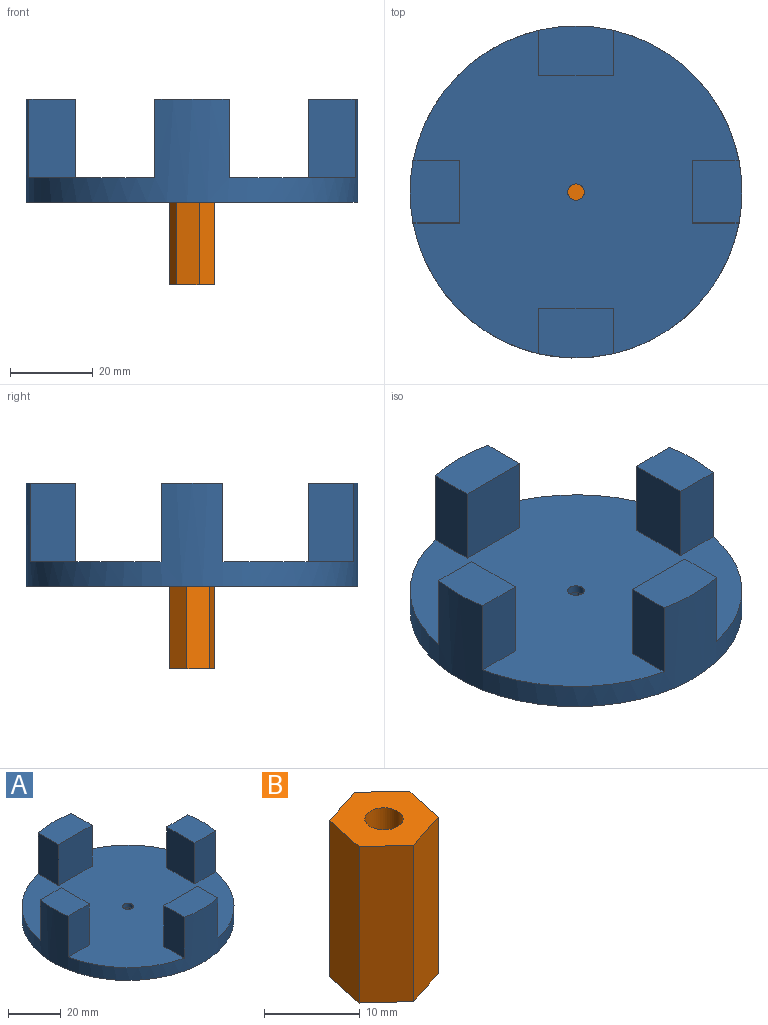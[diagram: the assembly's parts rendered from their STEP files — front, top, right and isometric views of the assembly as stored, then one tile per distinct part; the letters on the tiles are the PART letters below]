
ASSEMBLY  parts=2 mates=1
PART A: 27 faces, bbox 80.4x80.4x25 mm
  f0: plane 80.35x80.35mm, normal (0,0,-1), area 4987.5mm2, adj f2,f19,f20,f21,f22,f23,f24
  f1: plane 19x10.91mm, normal (1,0,0), area 207.2mm2, adj f2,f4,f5,f18
  f2: cylinder r=40.18mm len=80.35mm, axis (0,0,-1), area 2777.8mm2, adj f0,f1,f3,f5,f6,f8,f9,f10
  f3: plane 19x10.91mm, normal (-1,0,0), area 207.2mm2, adj f2,f4,f5,f18
  f4: plane 19x18mm, normal (0,-1,0), area 342mm2, adj f1,f3,f5,f18
  f5: plane 18x11.93mm, normal (0,0,1), area 208.6mm2, adj f1,f2,f3,f4
  f6: plane 19x10.91mm, normal (1,0,0), area 207.2mm2, adj f2,f7,f9,f18
  f7: plane 19x18mm, normal (0,1,0), area 342mm2, adj f6,f8,f9,f18
  f8: plane 19x10.91mm, normal (-1,0,0), area 207.2mm2, adj f2,f7,f9,f18
  f9: plane 18x11.93mm, normal (0,0,1), area 208.6mm2, adj f2,f6,f7,f8
  f10: plane 19x11.22mm, normal (0,1,0), area 213.2mm2, adj f2,f11,f13,f18
  f11: plane 19x15mm, normal (-1,0,0), area 285mm2, adj f10,f12,f13,f18
  f12: plane 19x11.22mm, normal (0,-1,0), area 213.2mm2, adj f2,f11,f13,f18
  f13: plane 15x11.93mm, normal (0,0,1), area 175.4mm2, adj f2,f10,f11,f12
  f14: plane 19x11.22mm, normal (0,1,0), area 213.2mm2, adj f2,f16,f17,f18
  f15: plane 19x11.22mm, normal (0,-1,0), area 213.2mm2, adj f2,f16,f17,f18
  f16: plane 19x15mm, normal (1,0,0), area 285mm2, adj f14,f15,f17,f18
  f17: plane 15x11.93mm, normal (0,0,1), area 175.4mm2, adj f2,f14,f15,f16
  f18: plane 78.94x78.31mm, normal (0,0,1), area 4290.6mm2, adj f1,f2,f3,f4,f6,f7,f8,f10
  f19: plane 5.41x4mm, normal (-0.3,-0.95,0), area 22.7mm2, adj f0,f20,f24,f25
  f20: plane 5.54x4mm, normal (-0.98,-0.21,0), area 22.7mm2, adj f0,f19,f21,f25
  f21: plane 4.19x4mm, normal (-0.67,0.74,0), area 22.7mm2, adj f0,f20,f22,f25
  f22: plane 5.41x4mm, normal (0.3,0.95,0), area 22.7mm2, adj f0,f21,f23,f25
  f23: plane 5.54x4mm, normal (0.98,0.21,0), area 22.7mm2, adj f0,f22,f24,f25
  f24: plane 4.19x4mm, normal (0.67,-0.74,0), area 22.7mm2, adj f0,f19,f23,f25
  f25: plane 11.08x10.81mm, normal (0,0,-1), area 71mm2, adj f19,f20,f21,f22,f23,f24,f26
  f26: cylinder r=2mm len=4mm, axis (0,0,-1), area 25.1mm2, adj f18,f25
PART B: 10 faces, bbox 10.8x11.1x20 mm
  f0: plane 20x5.41mm, normal (0.3,-0.95,0), area 113.4mm2, adj f1,f5,f6,f7
  f1: plane 20x5.54mm, normal (0.98,-0.21,0), area 113.4mm2, adj f0,f2,f6,f7
  f2: plane 20x4.19mm, normal (0.67,0.74,0), area 113.4mm2, adj f1,f3,f6,f7
  f3: plane 20x5.41mm, normal (-0.3,0.95,0), area 113.4mm2, adj f2,f4,f6,f7
  f4: plane 20x5.54mm, normal (-0.98,0.21,0), area 113.4mm2, adj f3,f5,f6,f7
  f5: plane 20x4.19mm, normal (-0.67,-0.74,0), area 113.4mm2, adj f0,f4,f6,f7
  f6: plane 11.08x10.81mm, normal (0,0,1), area 71mm2, adj f0,f1,f2,f3,f4,f5,f8
  f7: plane 11.08x10.81mm, normal (0,0,-1), area 83.6mm2, adj f0,f1,f2,f3,f4,f5
  f8: cylinder r=2mm len=10mm, axis (0,0,1), area 125.7mm2, adj f6,f9
  f9: plane 4x4mm, normal (0,0,1), area 12.6mm2, adj f8
PLACE A t=(-27.18,-7.67,-2.99)mm
PLACE B rot(axis=(0,0,-1),90deg) t=(-67.21,42.25,-22.99)mm
MATE fastened B.f8 <-> A.f2  axis (0,0,1) through (-27.18,-7.67,-2.99)mm
